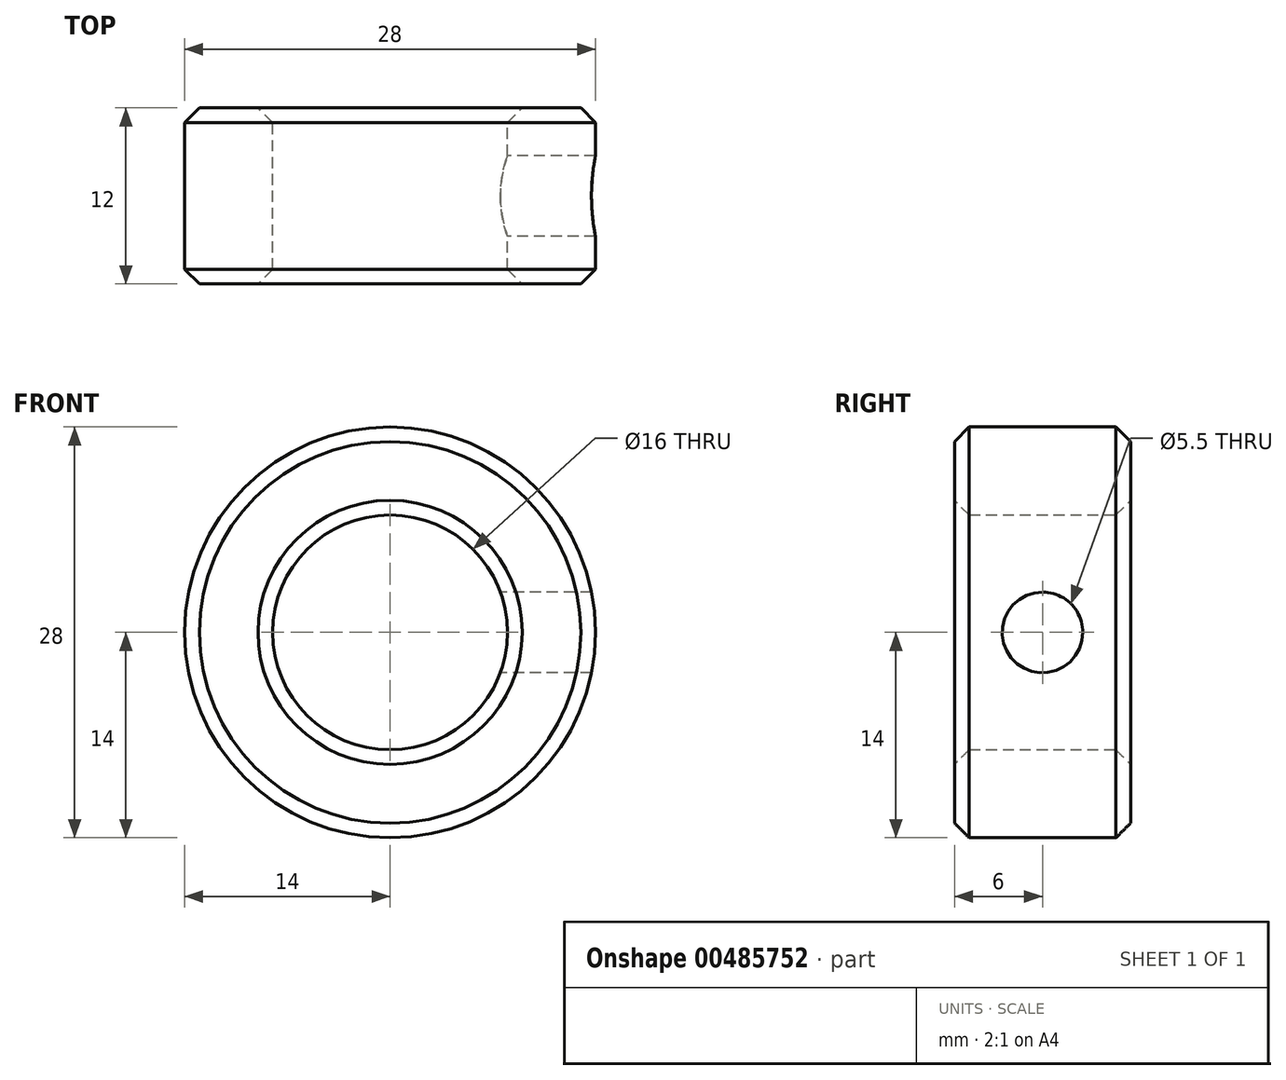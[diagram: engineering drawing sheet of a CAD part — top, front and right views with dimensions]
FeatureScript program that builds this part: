
annotation { "Feature Type Name" : "Feature", "Feature Type Description" : "" }
export const myFeature = defineFeature(function(context is Context, id is Id, definition is map)
    precondition{}
    {
        {
            assignVariable(context, id + "F0", {"name" : "Aussendurchmesser", "anyValue" : 28});
        }
        {
            var Q0;
            Q0=qCreatedBy(makeId("Front.planeOp"),FACE);
            var sketch = newSketch(context, id + "F1", { "sketchPlane" : qUnion([Q0])});
            skCircle(sketch, "E0", {"center": v(0, 0) * mm, "radius": 8 * mm});
            skCircle(sketch, "E1", {"center": v(0, 0) * mm, "radius": 14 * mm});
            skSolve(sketch);
        }
        {
            var Q0;
            Q0 = qSketchRegion(id + "F1", true);
            extrude(context, id + "F2", {"entities" : qUnion([Q0]), "depth" : 12 * mm});
        }
        {
            var Q0;
            Q0=makeQuery(id+"F2.opExtrude","SWEPT_FACE",FACE,{"disambiguationData":[OSD([sQuery(id+"F1.wireOp",EDGE,"E1")])]});
            var Q1;
            Q1=makeQuery(id+"F2.opExtrude","SWEPT_FACE",FACE,{"disambiguationData":[OSD([sQuery(id+"F1.wireOp",EDGE,"E0")])]});
            chamfer(context, id + "F3", {"entities" : qUnion([Q0, Q1]), "width" : 1 * mm, "tangentPropagation" : true});
        }
        {
            var Q0;
            Q0=qCreatedBy(makeId("Right.planeOp"),FACE);
            cPlane(context, id + "F4", {"entities" : qUnion([Q0]), "cplaneType" : CPlaneType.OFFSET, "offset" : (getVariable(context, 'Aussendurchmesser') / 2) * mm, "width" : 150 * mm, "height" : 150 * mm});
        }
        {
            var Q0;
            Q0=makeQuery(id+"F2.opExtrude","CAP_FACE",FACE,{"disambiguationData":[OSD([sQuery(id+"F1.wireOp",EDGE,"E0"),sQuery(id+"F1.wireOp",EDGE,"E1")])],"isStart":true});
            var Q1;
            Q1=makeQuery(id+"F2.opExtrude","CAP_FACE",FACE,{"disambiguationData":[OSD([sQuery(id+"F1.wireOp",EDGE,"E0"),sQuery(id+"F1.wireOp",EDGE,"E1")])],"isStart":false});
            cPlane(context, id + "F5", {"entities" : qUnion([Q0, Q1]), "cplaneType" : CPlaneType.MID_PLANE, "offset" : 25 * mm, "width" : 150 * mm, "height" : 150 * mm});
        }
        {
            var Q0;
            Q0=qCreatedBy(id+"F4.planeOp",FACE);
            var sketch = newSketch(context, id + "F6", { "sketchPlane" : qUnion([Q0])});
            skPoint(sketch, "E2", {"position": v(-6, 0) * mm});
            skSolve(sketch);
        }
        {
            var Q0;
            Q0=sQuery(id+"F6.wireOp",VERTEX,"E2");
            var Q1;
            Q1=makeQuery(id+"F2.opExtrude","SWEPT_BODY",BODY,{"disambiguationData":[OSD([sQuery(id+"F1.wireOp",EDGE,"E0"),sQuery(id+"F1.wireOp",EDGE,"E1")])]});
            hole(context, id + "F7", {"style" : HoleStyle.SIMPLE, "endStyle" : HoleEndStyle.BLIND, "standardTappedOrClearance" : lookupTablePath({ "standard" : "ISO", "fit" : "Normal", "size" : "M5", "type" : "Clearance" }), "standardBlindInLast" : lookupTablePath({ "fit" : "Standard", "standard" : "ISO", "size" : "M5", "type" : "Clearance" }), "holeDiameter" : 5.5 * mm, "holeDepth" : 14.4 * mm, "isTappedThrough" : true, "tappedDepth" : 12 * mm, "tapClearance" : 3, "locations" : qUnion([Q0]), "scope" : qUnion([Q1]), "startStyle" : HoleStartStyle.PART});
        }
    });
